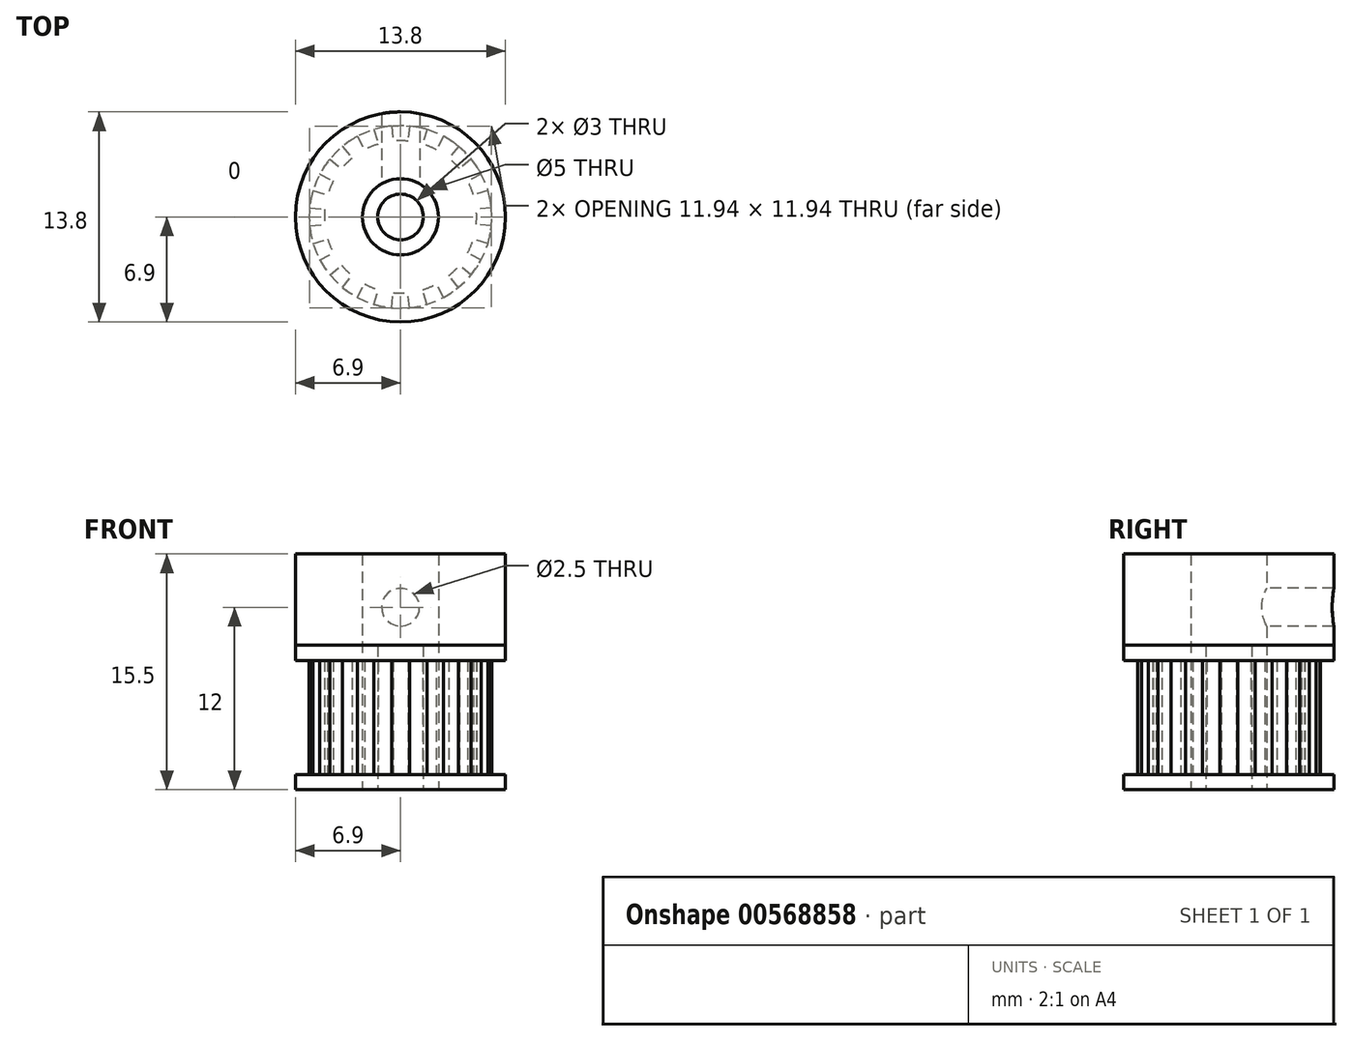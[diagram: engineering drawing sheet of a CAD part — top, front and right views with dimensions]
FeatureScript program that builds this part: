
annotation { "Feature Type Name" : "Feature", "Feature Type Description" : "" }
export const myFeature = defineFeature(function(context is Context, id is Id, definition is map)
    precondition{}
    {
        {
            var Q0;
            Q0=qCreatedBy(makeId("Top.planeOp"),FACE);
            var sketch = newSketch(context, id + "F0", { "sketchPlane" : qUnion([Q0])});
            skLineSegment(sketch, "E0", {"start": v(0, 0) * mm, "end": v(0, 20.7) * mm, "construction": true});
            skLineSegment(sketch, "E1", {"start": v(0, 0) * mm, "end": v(-4.04, 20.3) * mm, "construction": true});
            skCircle(sketch, "E2", {"center": v(0, 0) * mm, "radius": 6.9 * mm});
            skArc(sketch, "E3", {"start": v(0, 5) * mm, "mid": v(-0.25, 5) * mm, "end": v(-0.5, 4.98) * mm});
            skCircle(sketch, "E4", {"center": v(0, 0) * mm, "radius": 2.5 * mm});
            skArc(sketch, "E5", {"start": v(-0.59, 5.97) * mm, "mid": v(-0.88, 5.94) * mm, "end": v(-1.17, 5.88) * mm});
            skLineSegment(sketch, "E6", {"start": v(-0.59, 5.97) * mm, "end": v(-0.5, 4.98) * mm});
            skLineSegment(sketch, "E7.MirrorCS", {"start": v(0.59, 5.97) * mm, "end": v(0.5, 4.98) * mm});
            skArc(sketch, "E8.MirrorCS", {"start": v(0.59, 5.97) * mm, "mid": v(0.88, 5.94) * mm, "end": v(1.17, 5.88) * mm});
            skArc(sketch, "E9.MirrorCS", {"start": v(0, 5) * mm, "mid": v(0.25, 5) * mm, "end": v(0.5, 4.98) * mm});
            skArc(sketch, "E10.1.0", {"start": v(-1.74, 5.74) * mm, "mid": v(-1.46, 5.82) * mm, "end": v(-1.17, 5.88) * mm});
            skLineSegment(sketch, "E10.1.1", {"start": v(-1.74, 5.74) * mm, "end": v(-1.45, 4.78) * mm});
            skArc(sketch, "E10.1.2", {"start": v(-1.91, 4.62) * mm, "mid": v(-1.68, 4.7) * mm, "end": v(-1.45, 4.78) * mm});
            skArc(sketch, "E10.1.3", {"start": v(-1.91, 4.62) * mm, "mid": v(-2.14, 4.52) * mm, "end": v(-2.36, 4.4) * mm});
            skLineSegment(sketch, "E10.1.4", {"start": v(-2.83, 5.3) * mm, "end": v(-2.36, 4.4) * mm});
            skArc(sketch, "E10.1.5", {"start": v(-2.83, 5.3) * mm, "mid": v(-3.08, 5.15) * mm, "end": v(-3.33, 4.99) * mm});
            skArc(sketch, "E10.2.0", {"start": v(-3.8, 4.64) * mm, "mid": v(-3.57, 4.82) * mm, "end": v(-3.33, 4.99) * mm});
            skLineSegment(sketch, "E10.2.1", {"start": v(-3.8, 4.64) * mm, "end": v(-3.17, 3.87) * mm});
            skArc(sketch, "E10.2.2", {"start": v(-3.54, 3.54) * mm, "mid": v(-3.36, 3.7) * mm, "end": v(-3.17, 3.87) * mm});
            skArc(sketch, "E10.2.3", {"start": v(-3.54, 3.54) * mm, "mid": v(-3.7, 3.36) * mm, "end": v(-3.87, 3.17) * mm});
            skLineSegment(sketch, "E10.2.4", {"start": v(-4.64, 3.8) * mm, "end": v(-3.87, 3.17) * mm});
            skArc(sketch, "E10.2.5", {"start": v(-4.64, 3.8) * mm, "mid": v(-4.82, 3.57) * mm, "end": v(-4.99, 3.33) * mm});
            skArc(sketch, "E10.3.0", {"start": v(-5.3, 2.83) * mm, "mid": v(-5.15, 3.08) * mm, "end": v(-4.99, 3.33) * mm});
            skLineSegment(sketch, "E10.3.1", {"start": v(-5.3, 2.83) * mm, "end": v(-4.4, 2.36) * mm});
            skArc(sketch, "E10.3.2", {"start": v(-4.62, 1.91) * mm, "mid": v(-4.52, 2.14) * mm, "end": v(-4.4, 2.36) * mm});
            skArc(sketch, "E10.3.3", {"start": v(-4.62, 1.91) * mm, "mid": v(-4.7, 1.68) * mm, "end": v(-4.78, 1.45) * mm});
            skLineSegment(sketch, "E10.3.4", {"start": v(-5.74, 1.74) * mm, "end": v(-4.78, 1.45) * mm});
            skArc(sketch, "E10.3.5", {"start": v(-5.74, 1.74) * mm, "mid": v(-5.82, 1.46) * mm, "end": v(-5.88, 1.17) * mm});
            skArc(sketch, "E10.4.0", {"start": v(-5.97, 0.59) * mm, "mid": v(-5.94, 0.88) * mm, "end": v(-5.88, 1.17) * mm});
            skLineSegment(sketch, "E10.4.1", {"start": v(-5.97, 0.59) * mm, "end": v(-4.98, 0.5) * mm});
            skArc(sketch, "E10.4.2", {"start": v(-5, 0) * mm, "mid": v(-5, 0.25) * mm, "end": v(-4.98, 0.5) * mm});
            skArc(sketch, "E10.4.3", {"start": v(-5, 0) * mm, "mid": v(-5, -0.25) * mm, "end": v(-4.98, -0.5) * mm});
            skLineSegment(sketch, "E10.4.4", {"start": v(-5.97, -0.59) * mm, "end": v(-4.98, -0.5) * mm});
            skArc(sketch, "E10.4.5", {"start": v(-5.97, -0.59) * mm, "mid": v(-5.94, -0.88) * mm, "end": v(-5.88, -1.17) * mm});
            skArc(sketch, "E10.5.0", {"start": v(-5.74, -1.74) * mm, "mid": v(-5.82, -1.46) * mm, "end": v(-5.88, -1.17) * mm});
            skLineSegment(sketch, "E10.5.1", {"start": v(-5.74, -1.74) * mm, "end": v(-4.78, -1.45) * mm});
            skArc(sketch, "E10.5.2", {"start": v(-4.62, -1.91) * mm, "mid": v(-4.7, -1.68) * mm, "end": v(-4.78, -1.45) * mm});
            skArc(sketch, "E10.5.3", {"start": v(-4.62, -1.91) * mm, "mid": v(-4.52, -2.14) * mm, "end": v(-4.4, -2.36) * mm});
            skLineSegment(sketch, "E10.5.4", {"start": v(-5.3, -2.83) * mm, "end": v(-4.4, -2.36) * mm});
            skArc(sketch, "E10.5.5", {"start": v(-5.3, -2.83) * mm, "mid": v(-5.15, -3.08) * mm, "end": v(-4.99, -3.33) * mm});
            skArc(sketch, "E10.6.0", {"start": v(-4.64, -3.8) * mm, "mid": v(-4.82, -3.57) * mm, "end": v(-4.99, -3.33) * mm});
            skLineSegment(sketch, "E10.6.1", {"start": v(-4.64, -3.8) * mm, "end": v(-3.87, -3.17) * mm});
            skArc(sketch, "E10.6.2", {"start": v(-3.54, -3.54) * mm, "mid": v(-3.7, -3.36) * mm, "end": v(-3.87, -3.17) * mm});
            skArc(sketch, "E10.6.3", {"start": v(-3.54, -3.54) * mm, "mid": v(-3.36, -3.7) * mm, "end": v(-3.17, -3.87) * mm});
            skLineSegment(sketch, "E10.6.4", {"start": v(-3.8, -4.64) * mm, "end": v(-3.17, -3.87) * mm});
            skArc(sketch, "E10.6.5", {"start": v(-3.8, -4.64) * mm, "mid": v(-3.57, -4.82) * mm, "end": v(-3.33, -4.99) * mm});
            skArc(sketch, "E10.7.0", {"start": v(-2.83, -5.3) * mm, "mid": v(-3.08, -5.15) * mm, "end": v(-3.33, -4.99) * mm});
            skLineSegment(sketch, "E10.7.1", {"start": v(-2.83, -5.3) * mm, "end": v(-2.36, -4.4) * mm});
            skArc(sketch, "E10.7.2", {"start": v(-1.91, -4.62) * mm, "mid": v(-2.14, -4.52) * mm, "end": v(-2.36, -4.4) * mm});
            skArc(sketch, "E10.7.3", {"start": v(-1.91, -4.62) * mm, "mid": v(-1.68, -4.7) * mm, "end": v(-1.45, -4.78) * mm});
            skLineSegment(sketch, "E10.7.4", {"start": v(-1.74, -5.74) * mm, "end": v(-1.45, -4.78) * mm});
            skArc(sketch, "E10.7.5", {"start": v(-1.74, -5.74) * mm, "mid": v(-1.46, -5.82) * mm, "end": v(-1.17, -5.88) * mm});
            skArc(sketch, "E10.8.0", {"start": v(-0.59, -5.97) * mm, "mid": v(-0.88, -5.94) * mm, "end": v(-1.17, -5.88) * mm});
            skLineSegment(sketch, "E10.8.1", {"start": v(-0.59, -5.97) * mm, "end": v(-0.5, -4.98) * mm});
            skArc(sketch, "E10.8.2", {"start": v(0, -5) * mm, "mid": v(-0.25, -5) * mm, "end": v(-0.5, -4.98) * mm});
            skArc(sketch, "E10.8.3", {"start": v(0, -5) * mm, "mid": v(0.25, -5) * mm, "end": v(0.5, -4.98) * mm});
            skLineSegment(sketch, "E10.8.4", {"start": v(0.59, -5.97) * mm, "end": v(0.5, -4.98) * mm});
            skArc(sketch, "E10.8.5", {"start": v(0.59, -5.97) * mm, "mid": v(0.88, -5.94) * mm, "end": v(1.17, -5.88) * mm});
            skArc(sketch, "E10.9.0", {"start": v(1.74, -5.74) * mm, "mid": v(1.46, -5.82) * mm, "end": v(1.17, -5.88) * mm});
            skLineSegment(sketch, "E10.9.1", {"start": v(1.74, -5.74) * mm, "end": v(1.45, -4.78) * mm});
            skArc(sketch, "E10.9.2", {"start": v(1.91, -4.62) * mm, "mid": v(1.68, -4.7) * mm, "end": v(1.45, -4.78) * mm});
            skArc(sketch, "E10.9.3", {"start": v(1.91, -4.62) * mm, "mid": v(2.14, -4.52) * mm, "end": v(2.36, -4.4) * mm});
            skLineSegment(sketch, "E10.9.4", {"start": v(2.83, -5.3) * mm, "end": v(2.36, -4.4) * mm});
            skArc(sketch, "E10.9.5", {"start": v(2.83, -5.3) * mm, "mid": v(3.08, -5.15) * mm, "end": v(3.33, -4.99) * mm});
            skArc(sketch, "E10.10.0", {"start": v(3.8, -4.64) * mm, "mid": v(3.57, -4.82) * mm, "end": v(3.33, -4.99) * mm});
            skLineSegment(sketch, "E10.10.1", {"start": v(3.8, -4.64) * mm, "end": v(3.17, -3.87) * mm});
            skArc(sketch, "E10.10.2", {"start": v(3.54, -3.54) * mm, "mid": v(3.36, -3.7) * mm, "end": v(3.17, -3.87) * mm});
            skArc(sketch, "E10.10.3", {"start": v(3.54, -3.54) * mm, "mid": v(3.7, -3.36) * mm, "end": v(3.87, -3.17) * mm});
            skLineSegment(sketch, "E10.10.4", {"start": v(4.64, -3.8) * mm, "end": v(3.87, -3.17) * mm});
            skArc(sketch, "E10.10.5", {"start": v(4.64, -3.8) * mm, "mid": v(4.82, -3.57) * mm, "end": v(4.99, -3.33) * mm});
            skArc(sketch, "E10.11.0", {"start": v(5.3, -2.83) * mm, "mid": v(5.15, -3.08) * mm, "end": v(4.99, -3.33) * mm});
            skLineSegment(sketch, "E10.11.1", {"start": v(5.3, -2.83) * mm, "end": v(4.4, -2.36) * mm});
            skArc(sketch, "E10.11.2", {"start": v(4.62, -1.91) * mm, "mid": v(4.52, -2.14) * mm, "end": v(4.4, -2.36) * mm});
            skArc(sketch, "E10.11.3", {"start": v(4.62, -1.91) * mm, "mid": v(4.7, -1.68) * mm, "end": v(4.78, -1.45) * mm});
            skLineSegment(sketch, "E10.11.4", {"start": v(5.74, -1.74) * mm, "end": v(4.78, -1.45) * mm});
            skArc(sketch, "E10.11.5", {"start": v(5.74, -1.74) * mm, "mid": v(5.82, -1.46) * mm, "end": v(5.88, -1.17) * mm});
            skArc(sketch, "E10.12.0", {"start": v(5.97, -0.59) * mm, "mid": v(5.94, -0.88) * mm, "end": v(5.88, -1.17) * mm});
            skLineSegment(sketch, "E10.12.1", {"start": v(5.97, -0.59) * mm, "end": v(4.98, -0.5) * mm});
            skArc(sketch, "E10.12.2", {"start": v(5, 0) * mm, "mid": v(5, -0.25) * mm, "end": v(4.98, -0.5) * mm});
            skArc(sketch, "E10.12.3", {"start": v(5, 0) * mm, "mid": v(5, 0.25) * mm, "end": v(4.98, 0.5) * mm});
            skLineSegment(sketch, "E10.12.4", {"start": v(5.97, 0.59) * mm, "end": v(4.98, 0.5) * mm});
            skArc(sketch, "E10.12.5", {"start": v(5.97, 0.59) * mm, "mid": v(5.94, 0.88) * mm, "end": v(5.88, 1.17) * mm});
            skArc(sketch, "E10.13.0", {"start": v(5.74, 1.74) * mm, "mid": v(5.82, 1.46) * mm, "end": v(5.88, 1.17) * mm});
            skLineSegment(sketch, "E10.13.1", {"start": v(5.74, 1.74) * mm, "end": v(4.78, 1.45) * mm});
            skArc(sketch, "E10.13.2", {"start": v(4.62, 1.91) * mm, "mid": v(4.7, 1.68) * mm, "end": v(4.78, 1.45) * mm});
            skArc(sketch, "E10.13.3", {"start": v(4.62, 1.91) * mm, "mid": v(4.52, 2.14) * mm, "end": v(4.4, 2.36) * mm});
            skLineSegment(sketch, "E10.13.4", {"start": v(5.3, 2.83) * mm, "end": v(4.4, 2.36) * mm});
            skArc(sketch, "E10.13.5", {"start": v(5.3, 2.83) * mm, "mid": v(5.15, 3.08) * mm, "end": v(4.99, 3.33) * mm});
            skArc(sketch, "E10.14.0", {"start": v(4.64, 3.8) * mm, "mid": v(4.82, 3.57) * mm, "end": v(4.99, 3.33) * mm});
            skLineSegment(sketch, "E10.14.1", {"start": v(4.64, 3.8) * mm, "end": v(3.87, 3.17) * mm});
            skArc(sketch, "E10.14.2", {"start": v(3.54, 3.54) * mm, "mid": v(3.7, 3.36) * mm, "end": v(3.87, 3.17) * mm});
            skArc(sketch, "E10.14.3", {"start": v(3.54, 3.54) * mm, "mid": v(3.36, 3.7) * mm, "end": v(3.17, 3.87) * mm});
            skLineSegment(sketch, "E10.14.4", {"start": v(3.8, 4.64) * mm, "end": v(3.17, 3.87) * mm});
            skArc(sketch, "E10.14.5", {"start": v(3.8, 4.64) * mm, "mid": v(3.57, 4.82) * mm, "end": v(3.33, 4.99) * mm});
            skArc(sketch, "E10.15.0", {"start": v(2.83, 5.3) * mm, "mid": v(3.08, 5.15) * mm, "end": v(3.33, 4.99) * mm});
            skLineSegment(sketch, "E10.15.1", {"start": v(2.83, 5.3) * mm, "end": v(2.36, 4.4) * mm});
            skArc(sketch, "E10.15.2", {"start": v(1.91, 4.62) * mm, "mid": v(2.14, 4.52) * mm, "end": v(2.36, 4.4) * mm});
            skArc(sketch, "E10.15.3", {"start": v(1.91, 4.62) * mm, "mid": v(1.68, 4.7) * mm, "end": v(1.45, 4.78) * mm});
            skLineSegment(sketch, "E10.15.4", {"start": v(1.74, 5.74) * mm, "end": v(1.45, 4.78) * mm});
            skArc(sketch, "E10.15.5", {"start": v(1.74, 5.74) * mm, "mid": v(1.46, 5.82) * mm, "end": v(1.17, 5.88) * mm});
            skSolve(sketch);
        }
        {
            var Q0;
            Q0 = qSketchRegion(id + "F0", true);
            var Q1;
            Q1=makeQuery(id+"F0.imprint","IMPRINT",FACE,{"disambiguationData":[TD([[makeQuery(id+"F0.imprint","IMPRINT",EDGE,{"derivedFrom":sQuery(id+"F0.wireOp",EDGE,"E3")}),1.0]])]});
            extrude(context, id + "F1", {"entities" : qUnion([Q0, Q1]), "depth" : 15.5 * mm, "offsetDistance" : 25 * mm});
        }
        {
            var Q0;
            Q0=makeQuery(id+"F0.imprint","IMPRINT",FACE,{"disambiguationData":[TD([[makeQuery(id+"F0.imprint","IMPRINT",EDGE,{"derivedFrom":sQuery(id+"F0.wireOp",EDGE,"E2")}),1.0]])]});
            extrude(context, id + "F2", {"entities" : qUnion([Q0]), "operationType" : NewBodyOperationType.REMOVE, "depth" : 8.5 * mm, "offsetDistance" : 25 * mm, "hasSecondDirection" : true, "secondDirectionOppositeDirection" : false, "secondDirectionDepth" : 1 * mm});
        }
        {
            var Q0;
            Q0=qCreatedBy(makeId("Front.planeOp"),FACE);
            var sketch = newSketch(context, id + "F3", { "sketchPlane" : qUnion([Q0])});
            skCircle(sketch, "E11", {"center": v(0, 12) * mm, "radius": 1.25 * mm});
            skSolve(sketch);
        }
        {
            var Q0;
            Q0 = qSketchRegion(id + "F3", true);
            extrude(context, id + "F4", {"entities" : qUnion([Q0]), "operationType" : NewBodyOperationType.REMOVE, "oppositeDirection" : true, "depth" : 25 * mm, "offsetDistance" : 25 * mm});
        }
        {
            var Q0;
            Q0=qCreatedBy(makeId("Top.planeOp"),FACE);
            var sketch = newSketch(context, id + "F5", { "sketchPlane" : qUnion([Q0])});
            skCircle(sketch, "E12", {"center": v(0, 0) * mm, "radius": 1.5 * mm});
            skCircle(sketch, "E13.0", {"center": v(0, 0) * mm, "radius": 6.9 * mm});
            skCircle(sketch, "E14.converted", {"center": v(0, 0) * mm, "radius": 6 * mm});
            skSolve(sketch);
        }
        {
            var Q0;
            Q0=makeQuery(id+"F0.imprint","IMPRINT",FACE,{"disambiguationData":[TD([[makeQuery(id+"F0.imprint","IMPRINT",EDGE,{"derivedFrom":sQuery(id+"F0.wireOp",EDGE,"E2")}),1.0]])]});
            var Q1;
            Q1=makeQuery(id+"F0.imprint","IMPRINT",FACE,{"disambiguationData":[TD([[makeQuery(id+"F0.imprint","IMPRINT",EDGE,{"derivedFrom":sQuery(id+"F0.wireOp",EDGE,"E3")}),1.0]])]});
            var Q2;
            Q2=makeQuery(id+"F0.imprint","IMPRINT",FACE,{"disambiguationData":[TD([[makeQuery(id+"F0.imprint","IMPRINT",EDGE,{"derivedFrom":sQuery(id+"F0.wireOp",EDGE,"E4")}),1.0]])]});
            extrude(context, id + "F6", {"entities" : qUnion([Q0, Q1, Q2]), "depth" : 9.5 * mm, "offsetDistance" : 25 * mm});
        }
        {
            var Q0;
            Q0=makeQuery(id+"F0.imprint","IMPRINT",FACE,{"disambiguationData":[TD([[makeQuery(id+"F0.imprint","IMPRINT",EDGE,{"derivedFrom":sQuery(id+"F0.wireOp",EDGE,"E2")}),1.0]])]});
            extrude(context, id + "F7", {"entities" : qUnion([Q0]), "operationType" : NewBodyOperationType.REMOVE, "depth" : 8.5 * mm, "offsetDistance" : 25 * mm, "hasSecondDirection" : true, "secondDirectionOppositeDirection" : false, "secondDirectionDepth" : 1 * mm});
        }
        {
            var Q0;
            Q0=makeQuery(id+"F5.imprint","IMPRINT",FACE,{"disambiguationData":[TD([[makeQuery(id+"F5.imprint","IMPRINT",EDGE,{"derivedFrom":sQuery(id+"F5.wireOp",EDGE,"E12")}),1.0]])]});
            extrude(context, id + "F8", {"entities" : qUnion([Q0]), "operationType" : NewBodyOperationType.REMOVE, "depth" : 25 * mm, "offsetDistance" : 25 * mm});
        }
        {
            var Q0;
            Q0=makeQuery(id+"F5.imprint","IMPRINT",FACE,{"disambiguationData":[TD([[makeQuery(id+"F5.imprint","IMPRINT",EDGE,{"derivedFrom":sQuery(id+"F5.wireOp",EDGE,"E13.0")}),1.0]])]});
            var Q1;
            Q1=makeQuery(id+"F5.imprint","IMPRINT",FACE,{"disambiguationData":[TD([[makeQuery(id+"F5.imprint","IMPRINT",EDGE,{"derivedFrom":sQuery(id+"F5.wireOp",EDGE,"E12")}),-1.0]])]});
            extrude(context, id + "F9", {"entities" : qUnion([Q0, Q1]), "depth" : 9.5 * mm, "offsetDistance" : 25 * mm});
        }
        {
            var Q0;
            Q0=makeQuery(id+"F5.imprint","IMPRINT",FACE,{"disambiguationData":[TD([[makeQuery(id+"F5.imprint","IMPRINT",EDGE,{"derivedFrom":sQuery(id+"F5.wireOp",EDGE,"E13.0")}),1.0]])]});
            extrude(context, id + "F10", {"entities" : qUnion([Q0]), "operationType" : NewBodyOperationType.REMOVE, "depth" : 8.5 * mm, "offsetDistance" : 25 * mm, "hasSecondDirection" : true, "secondDirectionOppositeDirection" : false, "secondDirectionDepth" : 1 * mm});
        }
    });
